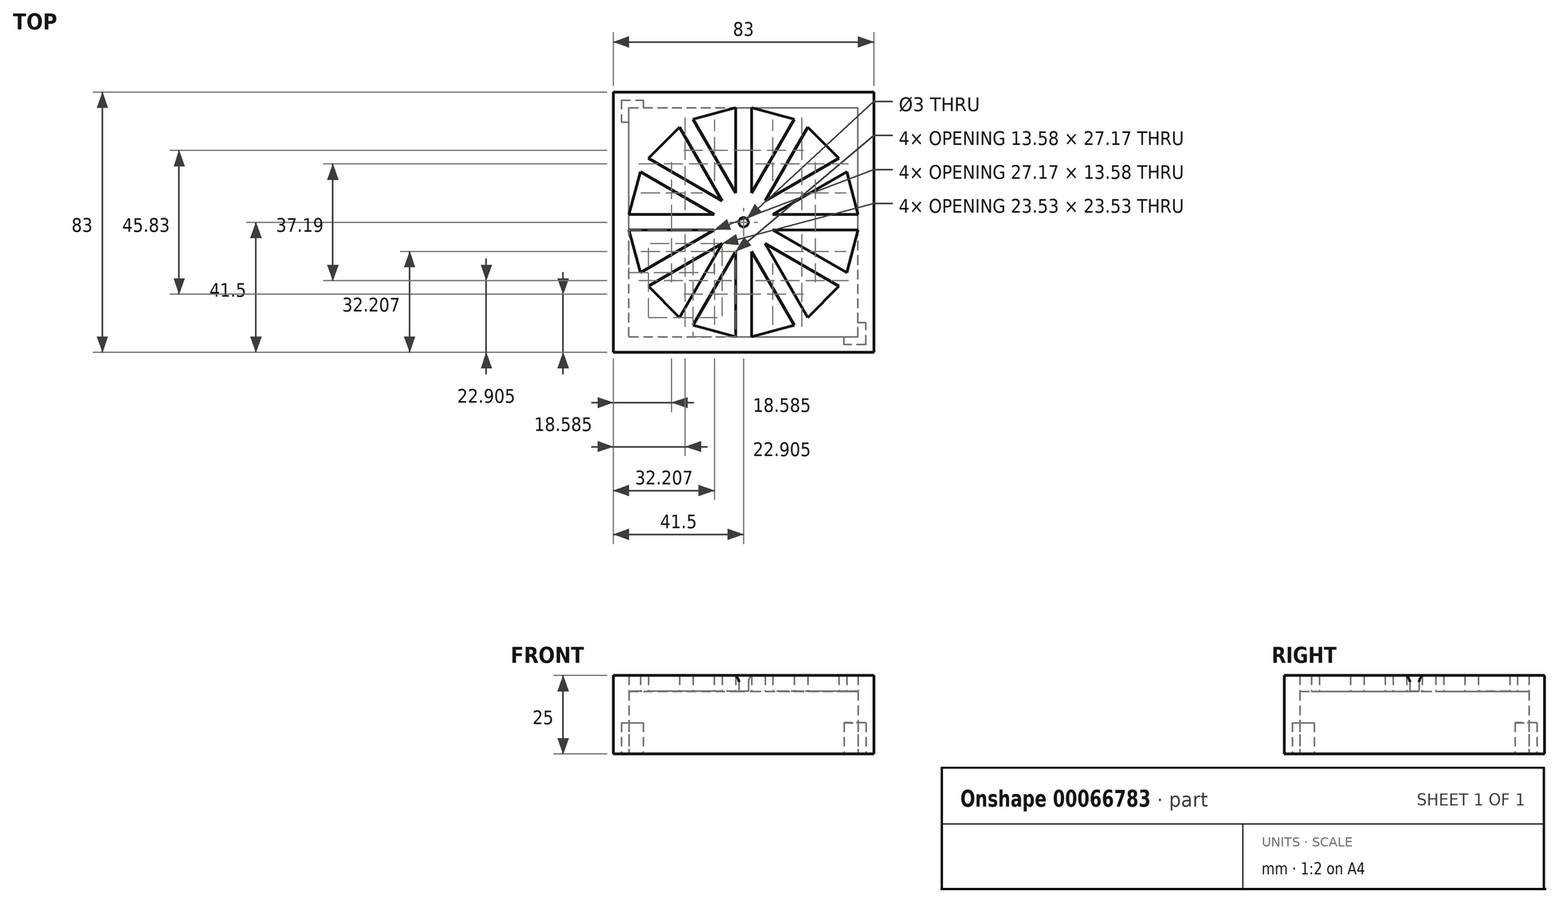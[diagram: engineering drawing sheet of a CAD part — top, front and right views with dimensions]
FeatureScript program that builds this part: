
annotation { "Feature Type Name" : "Feature", "Feature Type Description" : "" }
export const myFeature = defineFeature(function(context is Context, id is Id, definition is map)
    precondition{}
    {
        {
            var Q0;
            Q0=qCreatedBy(makeId("Top.planeOp"),FACE);
            var sketch = newSketch(context, id + "F0", { "sketchPlane" : qUnion([Q0])});
            skLineSegment(sketch, "E0.rect.bottom", {"start": v(-36.5, -36.5) * mm, "end": v(36.5, -36.5) * mm});
            skLineSegment(sketch, "E0.rect.top", {"start": v(-36.5, 36.5) * mm, "end": v(36.5, 36.5) * mm});
            skLineSegment(sketch, "E0.rect.left", {"start": v(-36.5, -36.5) * mm, "end": v(-36.5, 36.5) * mm});
            skLineSegment(sketch, "E0.rect.right", {"start": v(36.5, -36.5) * mm, "end": v(36.5, 36.5) * mm});
            skPoint(sketch, "E0.rect.middle", {"position": v(0, 0) * mm});
            skLineSegment(sketch, "E1.rect.bottom", {"start": v(-41.5, -41.5) * mm, "end": v(41.5, -41.5) * mm});
            skLineSegment(sketch, "E1.rect.top", {"start": v(-41.5, 41.5) * mm, "end": v(41.5, 41.5) * mm});
            skLineSegment(sketch, "E1.rect.left", {"start": v(-41.5, -41.5) * mm, "end": v(-41.5, 41.5) * mm});
            skLineSegment(sketch, "E1.rect.right", {"start": v(41.5, -41.5) * mm, "end": v(41.5, 41.5) * mm});
            skSolve(sketch);
        }
        {
            var Q0;
            Q0=makeQuery(id+"F0.imprint","IMPRINT",FACE,{"disambiguationData":[TD([[makeQuery(id+"F0.imprint","IMPRINT",EDGE,{"derivedFrom":sQuery(id+"F0.wireOp",EDGE,"E0.rect.bottom")}),-1.0]])]});
            extrude(context, id + "F1", {"entities" : qUnion([Q0]), "depth" : 20 * mm});
        }
        {
            var Q0;
            Q0=makeQuery(id+"F1.opExtrude","SWEPT_BODY",BODY,{"disambiguationData":[OSD([sQuery(id+"F0.wireOp",EDGE,"E0.rect.bottom"),sQuery(id+"F0.wireOp",EDGE,"E0.rect.top"),sQuery(id+"F0.wireOp",EDGE,"E0.rect.left"),sQuery(id+"F0.wireOp",EDGE,"E0.rect.right"),sQuery(id+"F0.wireOp",EDGE,"E1.rect.bottom"),sQuery(id+"F0.wireOp",EDGE,"E1.rect.top"),sQuery(id+"F0.wireOp",EDGE,"E1.rect.left"),sQuery(id+"F0.wireOp",EDGE,"E1.rect.right")])]});
            var Q1;
            Q1=qCreatedBy(makeId("Right.planeOp"),FACE);
            mirror(context, id + "F2", {"operationType" : NewBodyOperationType.ADD, "entities" : qUnion([Q0]), "mirrorPlane" : qUnion([Q1])});
        }
        {
            var Q0;
            Q0=makeQuery(id+"F1.opExtrude","CAP_FACE",FACE,{"disambiguationData":[OSD([sQuery(id+"F0.wireOp",EDGE,"E0.rect.bottom"),sQuery(id+"F0.wireOp",EDGE,"E0.rect.top"),sQuery(id+"F0.wireOp",EDGE,"E0.rect.left"),sQuery(id+"F0.wireOp",EDGE,"E0.rect.right"),sQuery(id+"F0.wireOp",EDGE,"E1.rect.bottom"),sQuery(id+"F0.wireOp",EDGE,"E1.rect.top"),sQuery(id+"F0.wireOp",EDGE,"E1.rect.left"),sQuery(id+"F0.wireOp",EDGE,"E1.rect.right")])],"isStart":true});
            var sketch = newSketch(context, id + "F3", { "sketchPlane" : qUnion([Q0])});
            skLineSegment(sketch, "E2.bottom", {"start": v(-41.5, -41.5) * mm, "end": v(-30, -41.5) * mm});
            skLineSegment(sketch, "E2.top", {"start": v(-41.5, -39) * mm, "end": v(-30, -39) * mm});
            skLineSegment(sketch, "E2.left", {"start": v(-41.5, -41.5) * mm, "end": v(-41.5, -39) * mm});
            skLineSegment(sketch, "E2.right", {"start": v(-30, -41.5) * mm, "end": v(-30, -39) * mm});
            skLineSegment(sketch, "E3.bottom", {"start": v(-41.5, -41.5) * mm, "end": v(-39, -41.5) * mm});
            skLineSegment(sketch, "E3.top", {"start": v(-41.5, -30) * mm, "end": v(-39, -30) * mm});
            skLineSegment(sketch, "E3.left", {"start": v(-41.5, -41.5) * mm, "end": v(-41.5, -30) * mm});
            skLineSegment(sketch, "E3.right", {"start": v(-39, -41.5) * mm, "end": v(-39, -30) * mm});
            skLineSegment(sketch, "E4.bottom", {"start": v(-30, -39) * mm, "end": v(-32, -39) * mm});
            skLineSegment(sketch, "E4.top", {"start": v(-30, -36.5) * mm, "end": v(-32, -36.5) * mm});
            skLineSegment(sketch, "E4.left", {"start": v(-30, -39) * mm, "end": v(-30, -36.5) * mm});
            skLineSegment(sketch, "E4.right", {"start": v(-32, -39) * mm, "end": v(-32, -36.5) * mm});
            skLineSegment(sketch, "E5.bottom", {"start": v(-39, -30) * mm, "end": v(-36.5, -30) * mm});
            skLineSegment(sketch, "E5.top", {"start": v(-39, -32) * mm, "end": v(-36.5, -32) * mm});
            skLineSegment(sketch, "E5.left", {"start": v(-39, -30) * mm, "end": v(-39, -32) * mm});
            skLineSegment(sketch, "E5.right", {"start": v(-36.5, -30) * mm, "end": v(-36.5, -32) * mm});
            skLineSegment(sketch, "E6.bottom", {"start": v(41.5, 41.5) * mm, "end": v(30, 41.5) * mm});
            skLineSegment(sketch, "E6.top", {"start": v(41.5, 39) * mm, "end": v(30, 39) * mm});
            skLineSegment(sketch, "E6.left", {"start": v(41.5, 41.5) * mm, "end": v(41.5, 39) * mm});
            skLineSegment(sketch, "E6.right", {"start": v(30, 41.5) * mm, "end": v(30, 39) * mm});
            skLineSegment(sketch, "E7.bottom", {"start": v(41.5, 41.5) * mm, "end": v(39, 41.5) * mm});
            skLineSegment(sketch, "E7.top", {"start": v(41.5, 30) * mm, "end": v(39, 30) * mm});
            skLineSegment(sketch, "E7.left", {"start": v(41.5, 41.5) * mm, "end": v(41.5, 30) * mm});
            skLineSegment(sketch, "E7.right", {"start": v(39, 41.5) * mm, "end": v(39, 30) * mm});
            skLineSegment(sketch, "E8.bottom", {"start": v(30, 39) * mm, "end": v(32, 39) * mm});
            skLineSegment(sketch, "E8.top", {"start": v(30, 36.5) * mm, "end": v(32, 36.5) * mm});
            skLineSegment(sketch, "E8.left", {"start": v(30, 39) * mm, "end": v(30, 36.5) * mm});
            skLineSegment(sketch, "E8.right", {"start": v(32, 39) * mm, "end": v(32, 36.5) * mm});
            skLineSegment(sketch, "E9.bottom", {"start": v(39, 30) * mm, "end": v(36.5, 30) * mm});
            skLineSegment(sketch, "E9.top", {"start": v(39, 32) * mm, "end": v(36.5, 32) * mm});
            skLineSegment(sketch, "E9.left", {"start": v(39, 30) * mm, "end": v(39, 32) * mm});
            skLineSegment(sketch, "E9.right", {"start": v(36.5, 30) * mm, "end": v(36.5, 32) * mm});
            skSolve(sketch);
        }
        {
            var Q0;
            {var subQ1=sQuery(id+"F3.wireOp",EDGE,"E8.right");Q0=makeQuery(id+"F3.imprint","IMPRINT",FACE,{"disambiguationData":[TD([[makeQuery(id+"F3.imprint","IMPRINT",EDGE,{"derivedFrom":subQ1}),1.0]])]});}
            var Q1;
            {var subQ1=sQuery(id+"F3.wireOp",EDGE,"E4.right");Q1=makeQuery(id+"F3.imprint","IMPRINT",FACE,{"disambiguationData":[TD([[makeQuery(id+"F3.imprint","IMPRINT",EDGE,{"derivedFrom":subQ1}),1.0]])]});}
            extrude(context, id + "F4", {"entities" : qUnion([Q0, Q1]), "operationType" : NewBodyOperationType.REMOVE, "oppositeDirection" : true, "depth" : 10 * mm});
        }
        {
            var Q0;
            Q0=makeQuery(id+"F1.opExtrude","CAP_FACE",FACE,{"disambiguationData":[OSD([sQuery(id+"F0.wireOp",EDGE,"E0.rect.bottom"),sQuery(id+"F0.wireOp",EDGE,"E0.rect.top"),sQuery(id+"F0.wireOp",EDGE,"E0.rect.left"),sQuery(id+"F0.wireOp",EDGE,"E0.rect.right"),sQuery(id+"F0.wireOp",EDGE,"E1.rect.bottom"),sQuery(id+"F0.wireOp",EDGE,"E1.rect.top"),sQuery(id+"F0.wireOp",EDGE,"E1.rect.left"),sQuery(id+"F0.wireOp",EDGE,"E1.rect.right")])],"isStart":false});
            var sketch = newSketch(context, id + "F5", { "sketchPlane" : qUnion([Q0])});
            skCircle(sketch, "E10", {"center": v(0, 0) * mm, "radius": 1.5 * mm});
            skLineSegment(sketch, "E11.bottom", {"start": v(36.5, -2.5) * mm, "end": v(9.33, -2.5) * mm});
            skLineSegment(sketch, "E11.top", {"start": v(36.5, 2.5) * mm, "end": v(9.33, 2.5) * mm});
            skLineSegment(sketch, "E12.left", {"start": v(2.5, -36.5) * mm, "end": v(2.5, -9.33) * mm});
            skLineSegment(sketch, "E12.right", {"start": v(-2.5, -36.5) * mm, "end": v(-2.5, -9.33) * mm});
            skLineSegment(sketch, "E13.1.0", {"start": v(-16.08, -32.86) * mm, "end": v(-2.5, -9.33) * mm});
            skLineSegment(sketch, "E13.1.1", {"start": v(-20.42, -30.36) * mm, "end": v(-6.83, -6.83) * mm});
            skLineSegment(sketch, "E13.1.2", {"start": v(32.86, -16.08) * mm, "end": v(9.33, -2.5) * mm});
            skLineSegment(sketch, "E13.1.3", {"start": v(30.36, -20.42) * mm, "end": v(6.83, -6.83) * mm});
            skLineSegment(sketch, "E13.2.0", {"start": v(-30.36, -20.42) * mm, "end": v(-6.83, -6.83) * mm});
            skLineSegment(sketch, "E13.2.1", {"start": v(-32.86, -16.08) * mm, "end": v(-9.33, -2.5) * mm});
            skLineSegment(sketch, "E13.2.2", {"start": v(20.42, -30.36) * mm, "end": v(6.83, -6.83) * mm});
            skLineSegment(sketch, "E13.2.3", {"start": v(16.08, -32.86) * mm, "end": v(2.5, -9.33) * mm});
            skLineSegment(sketch, "E14", {"start": v(-36.5, -2.5) * mm, "end": v(-32.86, -16.08) * mm});
            skLineSegment(sketch, "E15", {"start": v(-30.36, -20.42) * mm, "end": v(-20.42, -30.36) * mm});
            skLineSegment(sketch, "E16", {"start": v(-16.08, -32.86) * mm, "end": v(-2.5, -36.5) * mm});
            skLineSegment(sketch, "E17", {"start": v(2.5, -36.5) * mm, "end": v(16.08, -32.86) * mm});
            skLineSegment(sketch, "E18", {"start": v(20.42, -30.36) * mm, "end": v(30.36, -20.42) * mm});
            skLineSegment(sketch, "E19", {"start": v(32.86, -16.08) * mm, "end": v(36.5, -2.5) * mm});
            skLineSegment(sketch, "E20", {"start": v(36.5, 2.5) * mm, "end": v(32.86, 16.08) * mm});
            skLineSegment(sketch, "E21", {"start": v(30.36, 20.42) * mm, "end": v(20.42, 30.36) * mm});
            skLineSegment(sketch, "E22", {"start": v(16.08, 32.86) * mm, "end": v(2.5, 36.5) * mm});
            skLineSegment(sketch, "E23", {"start": v(-2.5, 36.5) * mm, "end": v(-16.08, 32.86) * mm});
            skLineSegment(sketch, "E24", {"start": v(-20.42, 30.36) * mm, "end": v(-30.36, 20.42) * mm});
            skLineSegment(sketch, "E25", {"start": v(-32.86, 16.08) * mm, "end": v(-36.5, 2.5) * mm});
            skLineSegment(sketch, "E26.trimOffspring", {"start": v(6.83, 6.83) * mm, "end": v(30.36, 20.42) * mm});
            skLineSegment(sketch, "E27.trimOffspring", {"start": v(6.83, 6.83) * mm, "end": v(20.42, 30.36) * mm});
            skLineSegment(sketch, "E28.trimOffspring", {"start": v(9.33, 2.5) * mm, "end": v(32.86, 16.08) * mm});
            skLineSegment(sketch, "E29.trimOffspring", {"start": v(-6.83, 6.83) * mm, "end": v(-20.42, 30.36) * mm});
            skLineSegment(sketch, "E30.trimOffspring", {"start": v(-6.83, 6.83) * mm, "end": v(-30.36, 20.42) * mm});
            skLineSegment(sketch, "E31.trimOffspring", {"start": v(-2.5, 9.33) * mm, "end": v(-16.08, 32.86) * mm});
            skLineSegment(sketch, "E32.trimOffspring", {"start": v(2.5, 9.33) * mm, "end": v(16.08, 32.86) * mm});
            skLineSegment(sketch, "E33.trimOffspring", {"start": v(2.5, 9.33) * mm, "end": v(2.5, 36.5) * mm});
            skLineSegment(sketch, "E34.trimOffspring", {"start": v(-9.33, 2.5) * mm, "end": v(-36.5, 2.5) * mm});
            skLineSegment(sketch, "E35.trimOffspring", {"start": v(-2.5, 9.33) * mm, "end": v(-2.5, 36.5) * mm});
            skLineSegment(sketch, "E36.trimOffspring", {"start": v(-9.33, 2.5) * mm, "end": v(-32.86, 16.08) * mm});
            skLineSegment(sketch, "E37.trimOffspring", {"start": v(-9.33, -2.5) * mm, "end": v(-36.5, -2.5) * mm});
            skLineSegment(sketch, "E38.bottom", {"start": v(-41.5, 41.5) * mm, "end": v(41.5, 41.5) * mm});
            skLineSegment(sketch, "E38.top", {"start": v(-41.5, -41.5) * mm, "end": v(41.5, -41.5) * mm});
            skLineSegment(sketch, "E38.left", {"start": v(-41.5, 41.5) * mm, "end": v(-41.5, -41.5) * mm});
            skLineSegment(sketch, "E38.right", {"start": v(41.5, 41.5) * mm, "end": v(41.5, -41.5) * mm});
            skSolve(sketch);
        }
        {
            var Q0;
            Q0=makeQuery(id+"F5.imprint","IMPRINT",FACE,{"disambiguationData":[TD([[makeQuery(id+"F5.imprint","IMPRINT",EDGE,{"derivedFrom":sQuery(id+"F5.wireOp",EDGE,"E38.bottom")}),-1.0]])]});
            var Q1;
            Q1=makeQuery(id+"F5.imprint","IMPRINT",FACE,{"disambiguationData":[TD([[makeQuery(id+"F5.imprint","IMPRINT",EDGE,{"derivedFrom":sQuery(id+"F5.wireOp",EDGE,"E10")}),-1.0]])]});
            extrude(context, id + "F6", {"entities" : qUnion([Q0, Q1]), "operationType" : NewBodyOperationType.ADD, "depth" : 5 * mm});
        }
        {
            var Q0;
            Q0=makeQuery(id+"F6.opExtrude","CAP_EDGE",EDGE,{"disambiguationData":[OSD([sQuery(id+"F5.wireOp",EDGE,"E10")])],"isStart":false});
            fillet(context, id + "F7", {"entities" : qUnion([Q0]), "radius" : 2 * mm, "tangentPropagation" : true, "allowEdgeOverflow" : false});
        }
    });
